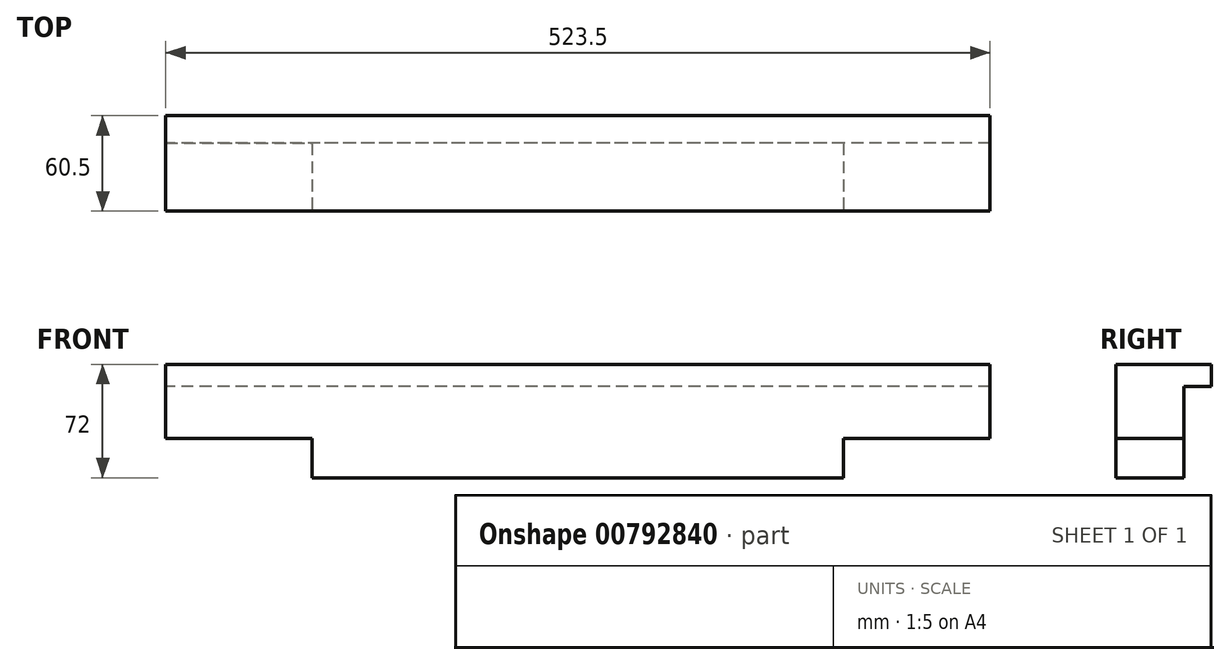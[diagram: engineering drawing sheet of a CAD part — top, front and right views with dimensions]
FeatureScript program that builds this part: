
annotation { "Feature Type Name" : "Feature", "Feature Type Description" : "" }
export const myFeature = defineFeature(function(context is Context, id is Id, definition is map)
    precondition{}
    {
        {
            var Q0;
            Q0=qCreatedBy(makeId("Front.planeOp"),FACE);
            var sketch = newSketch(context, id + "F0", { "sketchPlane" : qUnion([Q0])});
            skLineSegment(sketch, "E0.bottom", {"start": v(261.75, -36) * mm, "end": v(-261.75, -36) * mm});
            skLineSegment(sketch, "E0.top", {"start": v(261.75, 36) * mm, "end": v(-261.75, 36) * mm});
            skLineSegment(sketch, "E0.left", {"start": v(261.75, -36) * mm, "end": v(261.75, 36) * mm});
            skLineSegment(sketch, "E0.right", {"start": v(-261.75, -36) * mm, "end": v(-261.75, 36) * mm});
            skPoint(sketch, "E0.middle", {"position": v(0, 0) * mm});
            skSolve(sketch);
        }
        {
            var Q0;
            Q0 = qSketchRegion(id + "F0", true);
            extrude(context, id + "F1", {"entities" : qUnion([Q0]), "depth" : 43 * mm, "offsetDistance" : 25 * mm});
        }
        {
            var Q0;
            Q0=makeQuery(id+"F1.opExtrude","CAP_FACE",FACE,{"disambiguationData":[OSD([sQuery(id+"F0.wireOp",EDGE,"E0.bottom"),sQuery(id+"F0.wireOp",EDGE,"E0.top"),sQuery(id+"F0.wireOp",EDGE,"E0.left"),sQuery(id+"F0.wireOp",EDGE,"E0.right")])],"isStart":false});
            var sketch = newSketch(context, id + "F2", { "sketchPlane" : qUnion([Q0])});
            skLineSegment(sketch, "E1.bottom", {"start": v(-261.75, -11) * mm, "end": v(-168.75, -11) * mm});
            skLineSegment(sketch, "E1.top", {"start": v(-261.75, -36) * mm, "end": v(-168.75, -36) * mm});
            skLineSegment(sketch, "E1.left", {"start": v(-261.75, -11) * mm, "end": v(-261.75, -36) * mm});
            skLineSegment(sketch, "E1.right", {"start": v(-168.75, -11) * mm, "end": v(-168.75, -36) * mm});
            skLineSegment(sketch, "E2.bottom", {"start": v(261.75, -36) * mm, "end": v(168.75, -36) * mm});
            skLineSegment(sketch, "E2.top", {"start": v(261.75, -11) * mm, "end": v(168.75, -11) * mm});
            skLineSegment(sketch, "E2.left", {"start": v(261.75, -36) * mm, "end": v(261.75, -11) * mm});
            skLineSegment(sketch, "E2.right", {"start": v(168.75, -36) * mm, "end": v(168.75, -11) * mm});
            skSolve(sketch);
        }
        {
            var Q0;
            Q0 = qSketchRegion(id + "F2", true);
            extrude(context, id + "F3", {"entities" : qUnion([Q0]), "operationType" : NewBodyOperationType.REMOVE, "oppositeDirection" : true, "depth" : 93 * mm, "offsetDistance" : 25 * mm});
        }
        {
            var Q0;
            Q0=makeQuery(id+"F1.opExtrude","CAP_FACE",FACE,{"disambiguationData":[OSD([sQuery(id+"F0.wireOp",EDGE,"E0.bottom"),sQuery(id+"F0.wireOp",EDGE,"E0.top"),sQuery(id+"F0.wireOp",EDGE,"E0.left"),sQuery(id+"F0.wireOp",EDGE,"E0.right")])],"isStart":true});
            var sketch = newSketch(context, id + "F4", { "sketchPlane" : qUnion([Q0])});
            skLineSegment(sketch, "E3.bottom", {"start": v(-261.75, 36) * mm, "end": v(261.75, 36) * mm});
            skLineSegment(sketch, "E3.top", {"start": v(-261.75, 22) * mm, "end": v(261.75, 22) * mm});
            skLineSegment(sketch, "E3.left", {"start": v(-261.75, 36) * mm, "end": v(-261.75, 22) * mm});
            skLineSegment(sketch, "E3.right", {"start": v(261.75, 36) * mm, "end": v(261.75, 22) * mm});
            skSolve(sketch);
        }
        {
            var Q0;
            Q0 = qSketchRegion(id + "F4", true);
            extrude(context, id + "F5", {"entities" : qUnion([Q0]), "operationType" : NewBodyOperationType.ADD, "depth" : 17.5 * mm, "offsetDistance" : 25 * mm});
        }
    });
